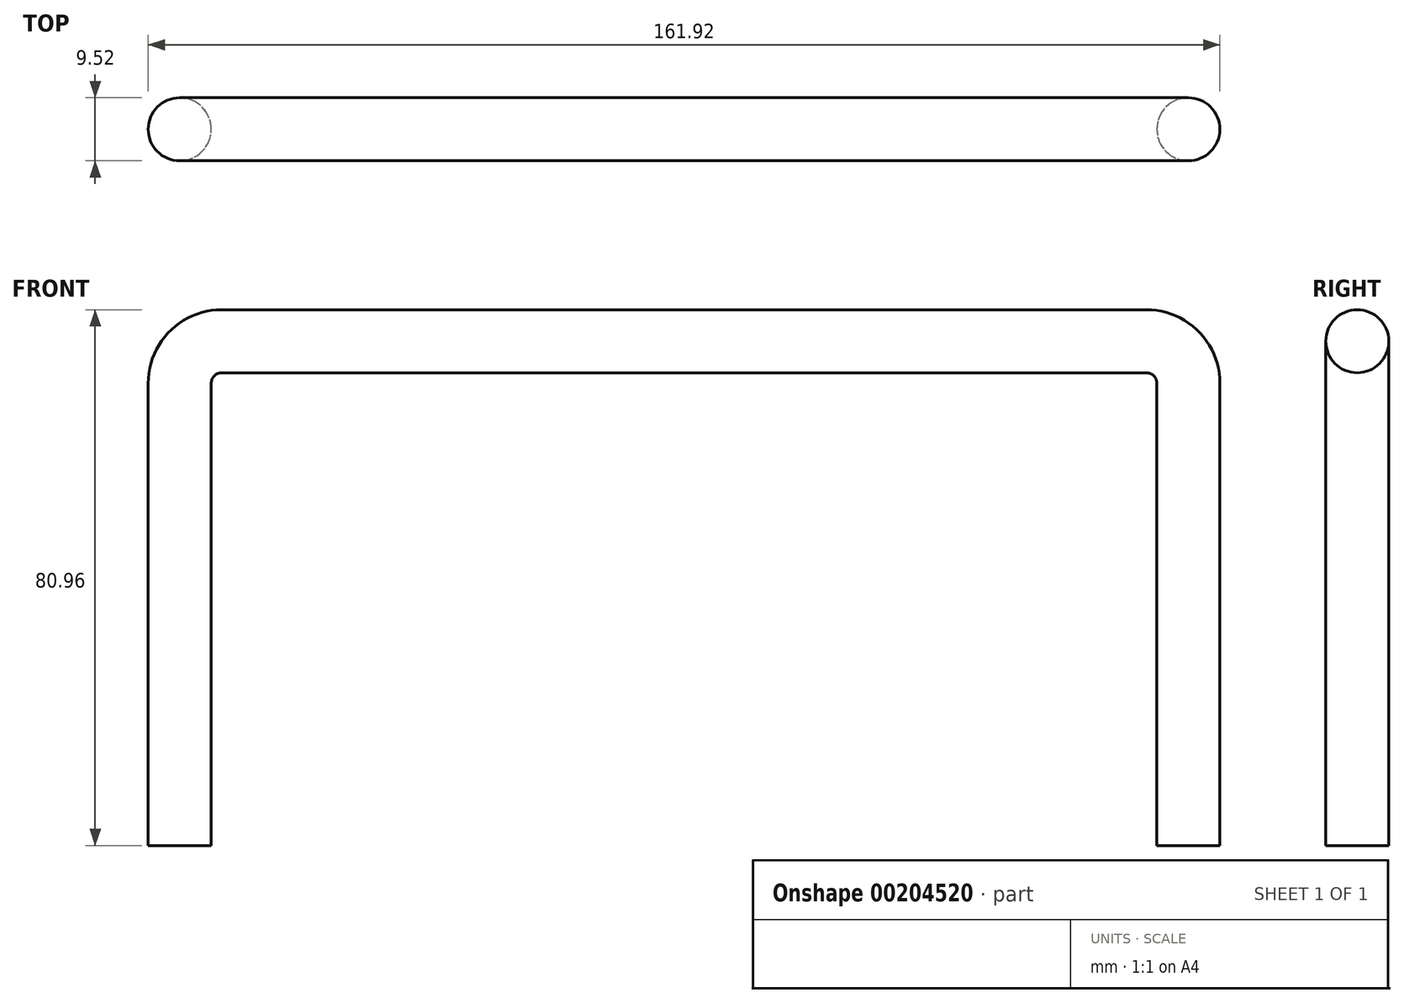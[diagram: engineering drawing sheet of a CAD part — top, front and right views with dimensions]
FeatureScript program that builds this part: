
annotation { "Feature Type Name" : "Feature", "Feature Type Description" : "" }
export const myFeature = defineFeature(function(context is Context, id is Id, definition is map)
    precondition{}
    {
        {
            var Q0;
            Q0=qCreatedBy(makeId("Top.planeOp"),FACE);
            var sketch = newSketch(context, id + "F0", { "sketchPlane" : qUnion([Q0])});
            skCircle(sketch, "E0", {"center": v(76.2, 0) * mm, "radius": 4.76 * mm});
            skSolve(sketch);
        }
        {
            var Q0;
            Q0=qCreatedBy(makeId("Front.planeOp"),FACE);
            var sketch = newSketch(context, id + "F1", { "sketchPlane" : qUnion([Q0])});
            skLineSegment(sketch, "E1", {"start": v(76.2, 0) * mm, "end": v(76.2, 69.85) * mm});
            skLineSegment(sketch, "E2", {"start": v(69.85, 76.2) * mm, "end": v(0, 76.2) * mm});
            skPoint(sketch, "E3.visualSharp", {"position": v(76.2, 76.2) * mm});
            skArc(sketch, "E3.filletArc", {"start": v(76.2, 69.85) * mm, "mid": v(74.34, 74.34) * mm, "end": v(69.85, 76.2) * mm});
            skLineSegment(sketch, "E4.MirrorCS", {"start": v(-69.85, 76.2) * mm, "end": v(0, 76.2) * mm});
            skLineSegment(sketch, "E5.MirrorCS", {"start": v(-76.2, 0) * mm, "end": v(-76.2, 69.85) * mm});
            skArc(sketch, "E6.MirrorCS", {"start": v(-76.2, 69.85) * mm, "mid": v(-74.34, 74.34) * mm, "end": v(-69.85, 76.2) * mm});
            skSolve(sketch);
        }
        {
            var Q0;
            Q0=makeQuery(id+"F0.imprint","IMPRINT",FACE,{"disambiguationData":[TD([[makeQuery(id+"F0.imprint","IMPRINT",EDGE,{"derivedFrom":sQuery(id+"F0.wireOp",EDGE,"E0")}),1.0]])]});
            var Q1;
            Q1=sQuery(id+"F1.wireOp",EDGE,"E1");
            var Q2;
            Q2=sQuery(id+"F1.wireOp",EDGE,"E3.filletArc");
            var Q3;
            Q3=sQuery(id+"F1.wireOp",EDGE,"E2");
            var Q4;
            Q4=sQuery(id+"F1.wireOp",EDGE,"E4.MirrorCS");
            var Q5;
            Q5=sQuery(id+"F1.wireOp",EDGE,"E6.MirrorCS");
            var Q6;
            Q6=sQuery(id+"F1.wireOp",EDGE,"E5.MirrorCS");
            sweep(context, id + "F2", {"profiles" : qUnion([Q0]), "path" : qUnion([Q1, Q2, Q3, Q4, Q5, Q6])});
        }
    });
